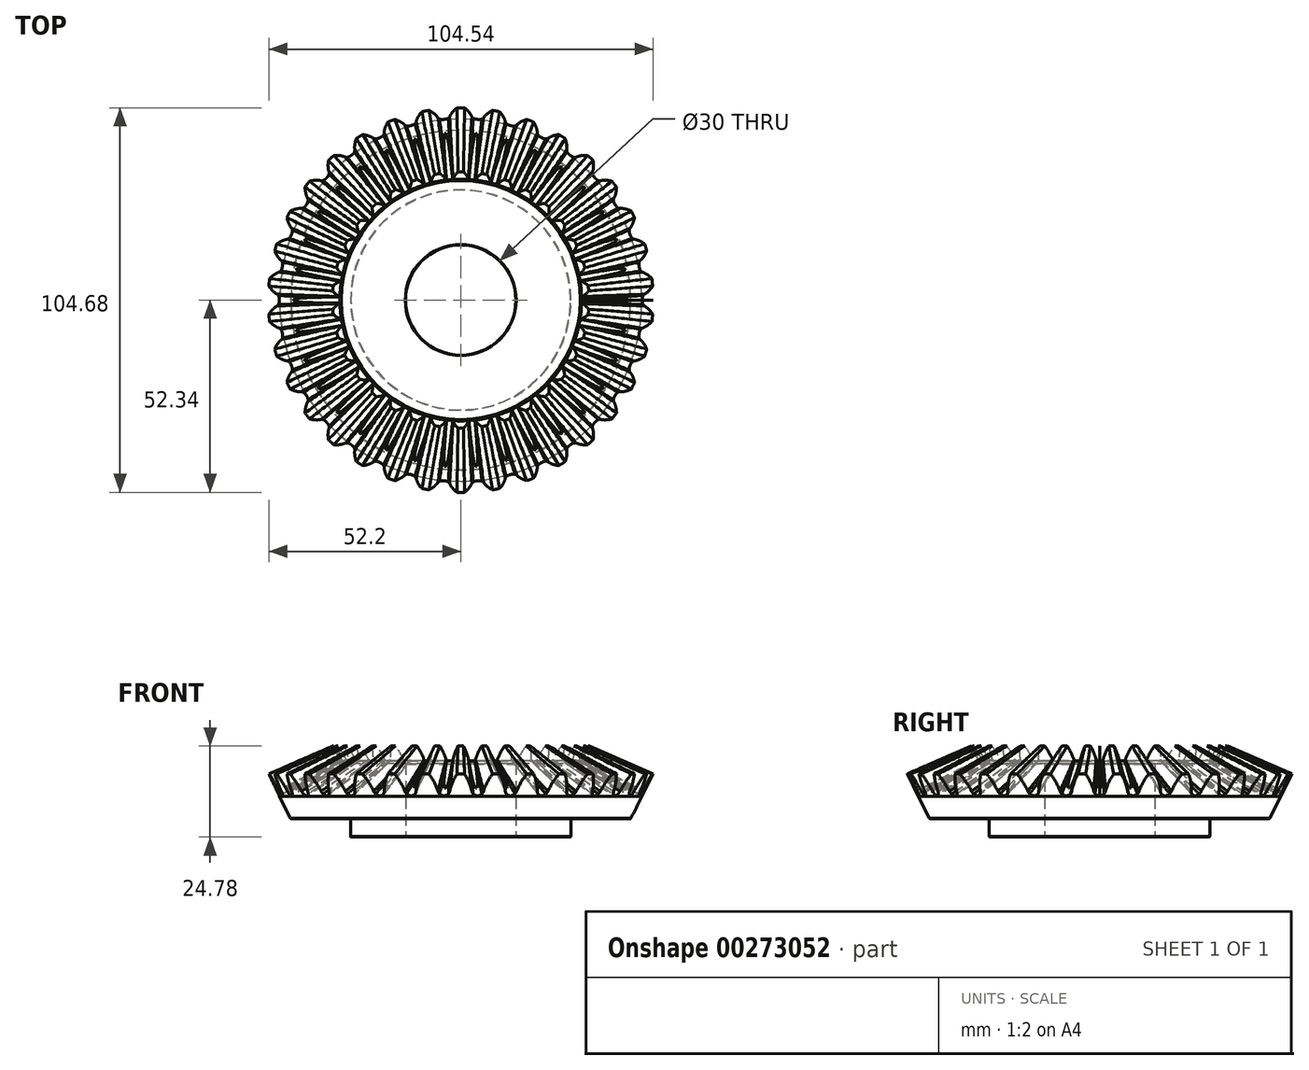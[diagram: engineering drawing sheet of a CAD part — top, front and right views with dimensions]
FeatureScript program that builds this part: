
annotation { "Feature Type Name" : "Feature", "Feature Type Description" : "" }
export const myFeature = defineFeature(function(context is Context, id is Id, definition is map)
    precondition{}
    {
        {
            var Q0;
            Q0=qCreatedBy(makeId("Front.planeOp"),FACE);
            var sketch = newSketch(context, id + "F0", { "sketchPlane" : qUnion([Q0])});
            skLineSegment(sketch, "E0", {"start": v(0, 35) * mm, "end": v(57.54, 6.23) * mm, "construction": true});
            skLineSegment(sketch, "E1", {"start": v(0, 35) * mm, "end": v(0, 0) * mm, "construction": true});
            skLineSegment(sketch, "E2", {"start": v(32.89, 15.76) * mm, "end": v(49.32, 6.14) * mm});
            skLineSegment(sketch, "E3", {"start": v(0, 0) * mm, "end": v(46.25, 0) * mm, "construction": true});
            skLineSegment(sketch, "E4", {"start": v(49.32, 6.14) * mm, "end": v(52.35, 12.18) * mm});
            skLineSegment(sketch, "E5", {"start": v(52.34, 12.18) * mm, "end": v(34.9, 19.78) * mm});
            skLineSegment(sketch, "E6", {"start": v(32.5, 15) * mm, "end": v(0, 15) * mm, "construction": true});
            skLineSegment(sketch, "E7", {"start": v(49.32, 6.14) * mm, "end": v(46.25, 0) * mm, "construction": true});
            skLineSegment(sketch, "E8", {"start": v(32.89, 15.76) * mm, "end": v(32.5, 15) * mm, "construction": true});
            skLineSegment(sketch, "E9", {"start": v(34.9, 19.78) * mm, "end": v(32.89, 15.76) * mm});
            skSolve(sketch);
        }
        {
            var Q0;
            Q0 = qSketchRegion(id + "F0", true);
            var Q1;
            Q1=sQuery(id+"F0.wireOp",EDGE,"E1");
            revolve(context, id + "F1", {"entities" : qUnion([Q0]), "axis" : qUnion([Q1]), "revolveType" : RevolveType.FULL});
        }
        {
            var Q0;
            Q0=qCreatedBy(makeId("Front.planeOp"),FACE);
            var sketch = newSketch(context, id + "F2", { "sketchPlane" : qUnion([Q0])});
            skLineSegment(sketch, "E10", {"start": v(0, 35) * mm, "end": v(0, 0) * mm, "construction": true});
            skLineSegment(sketch, "E11", {"start": v(0, 0) * mm, "end": v(46.25, 0) * mm});
            skLineSegment(sketch, "E12", {"start": v(32.5, 15) * mm, "end": v(0, 15) * mm});
            skLineSegment(sketch, "E13", {"start": v(49.32, 6.14) * mm, "end": v(46.25, 0) * mm});
            skLineSegment(sketch, "E14", {"start": v(32.89, 15.76) * mm, "end": v(32.5, 15) * mm});
            skLineSegment(sketch, "E15", {"start": v(32.89, 15.76) * mm, "end": v(49.32, 6.14) * mm});
            skLineSegment(sketch, "E16", {"start": v(0, 15) * mm, "end": v(0, 0) * mm});
            skSolve(sketch);
        }
        {
            var Q0;
            Q0 = qSketchRegion(id + "F2", true);
            var Q1;
            Q1=sQuery(id+"F2.wireOp",EDGE,"E10");
            revolve(context, id + "F3", {"entities" : qUnion([Q0]), "axis" : qUnion([Q1]), "revolveType" : RevolveType.FULL});
        }
        {
            var Q0;
            Q0 = qSketchRegion(id + "F0", true);
            extrude(context, id + "F4", {"entities" : qUnion([Q0]), "depth" : 0.01 * mm, "hasSecondDirection" : true, "secondDirectionOppositeDirection" : true, "secondDirectionDepth" : 0.01 * mm});
        }
        {
            var Q0;
            Q0=makeQuery(id+"F4.opExtrude","SWEPT_FACE",FACE,{"disambiguationData":[OSD([sQuery(id+"F0.wireOp",EDGE,"E4")])]});
            cPlane(context, id + "F5", {"entities" : qUnion([Q0]), "cplaneType" : CPlaneType.OFFSET, "offset" : 0 * mm, "width" : 150 * mm, "height" : 150 * mm});
        }
        {
            var Q0;
            Q0=qCreatedBy(id+"F5.planeOp",FACE);
            var sketch = newSketch(context, id + "F6", { "sketchPlane" : qUnion([Q0])});
            skPoint(sketch, "E17.center", {"position": v(0, 0) * mm});
            skLineSegment(sketch, "E17.anchor2", {"start": v(0, 0) * mm, "end": v(0, 27.7) * mm, "construction": true});
            skLineSegment(sketch, "E18", {"start": v(0, 27.7) * mm, "end": v(0, 34.3) * mm, "construction": true});
            skLineSegment(sketch, "E19", {"start": v(-3.86, 34.3) * mm, "end": v(3.86, 34.3) * mm});
            skLineSegment(sketch, "E20", {"start": v(-0.18, 27.69) * mm, "end": v(0.18, 27.69) * mm});
            skArc(sketch, "E21", {"start": v(-1.58, 28.95) * mm, "mid": v(-2.5, 31.72) * mm, "end": v(-3.86, 34.3) * mm});
            skArc(sketch, "E22", {"start": v(-1.6, 29.04) * mm, "mid": v(-1.37, 28.44) * mm, "end": v(-0.96, 27.95) * mm});
            skArc(sketch, "E23", {"start": v(-1.21, 28.2) * mm, "mid": v(-0.76, 27.83) * mm, "end": v(-0.18, 27.69) * mm});
            skArc(sketch, "E24.MirrorCS", {"start": v(1.21, 28.2) * mm, "mid": v(0.76, 27.83) * mm, "end": v(0.18, 27.69) * mm});
            skArc(sketch, "E25.MirrorCS", {"start": v(1.6, 29.04) * mm, "mid": v(1.37, 28.44) * mm, "end": v(0.96, 27.95) * mm});
            skArc(sketch, "E26.MirrorCS", {"start": v(1.58, 28.95) * mm, "mid": v(2.5, 31.72) * mm, "end": v(3.86, 34.3) * mm});
            skSolve(sketch);
        }
        {
            var Q0;
            Q0 = qSketchRegion(id + "F6", true);
            extrude(context, id + "F7", {"entities" : qUnion([Q0]), "oppositeDirection" : true, "depth" : 20 * mm, "hasDraft" : true, "draftAngle" : 2 * degree, "draftPullDirection" : true});
        }
        {
            var Q0;
            Q0=makeQuery(id+"F7.opExtrude","SWEPT_BODY",BODY,{"disambiguationData":[OSD([sQuery(id+"F6.wireOp",EDGE,"E19"),sQuery(id+"F6.wireOp",EDGE,"E20"),sQuery(id+"F6.wireOp",EDGE,"E21"),sQuery(id+"F6.wireOp",EDGE,"E22"),sQuery(id+"F6.wireOp",EDGE,"E23"),sQuery(id+"F6.wireOp",EDGE,"E24.MirrorCS"),sQuery(id+"F6.wireOp",EDGE,"E25.MirrorCS"),sQuery(id+"F6.wireOp",EDGE,"E26.MirrorCS")])]});
            var Q1;
            Q1=makeQuery(id+"F3.opRevolve","SWEPT_EDGE",EDGE,{"disambiguationData":[OSD([sQuery(id+"F2.wireOp",EDGE,"E11"),sQuery(id+"F2.wireOp",EDGE,"E13")])]});
            circularPattern(context, id + "F8", {"entities" : qUnion([Q0]), "axis" : qUnion([Q1]), "angle" : 360 * degree, "instanceCount" : 34, "equalSpace" : true});
        }
        {
            var Q0;
            Q0=makeQuery(id+"F8.opPattern","COPY",BODY,{"derivedFrom":makeQuery(id+"F7.opExtrude","SWEPT_BODY",BODY,{"disambiguationData":[OSD([sQuery(id+"F6.wireOp",EDGE,"E19"),sQuery(id+"F6.wireOp",EDGE,"E20"),sQuery(id+"F6.wireOp",EDGE,"E21"),sQuery(id+"F6.wireOp",EDGE,"E22"),sQuery(id+"F6.wireOp",EDGE,"E23"),sQuery(id+"F6.wireOp",EDGE,"E24.MirrorCS"),sQuery(id+"F6.wireOp",EDGE,"E25.MirrorCS"),sQuery(id+"F6.wireOp",EDGE,"E26.MirrorCS")])]}),"instanceName":"26"});
            var Q1;
            Q1=makeQuery(id+"F8.opPattern","COPY",BODY,{"derivedFrom":makeQuery(id+"F7.opExtrude","SWEPT_BODY",BODY,{"disambiguationData":[OSD([sQuery(id+"F6.wireOp",EDGE,"E19"),sQuery(id+"F6.wireOp",EDGE,"E20"),sQuery(id+"F6.wireOp",EDGE,"E21"),sQuery(id+"F6.wireOp",EDGE,"E22"),sQuery(id+"F6.wireOp",EDGE,"E23"),sQuery(id+"F6.wireOp",EDGE,"E24.MirrorCS"),sQuery(id+"F6.wireOp",EDGE,"E25.MirrorCS"),sQuery(id+"F6.wireOp",EDGE,"E26.MirrorCS")])]}),"instanceName":"27"});
            var Q2;
            Q2=makeQuery(id+"F8.opPattern","COPY",BODY,{"derivedFrom":makeQuery(id+"F7.opExtrude","SWEPT_BODY",BODY,{"disambiguationData":[OSD([sQuery(id+"F6.wireOp",EDGE,"E19"),sQuery(id+"F6.wireOp",EDGE,"E20"),sQuery(id+"F6.wireOp",EDGE,"E21"),sQuery(id+"F6.wireOp",EDGE,"E22"),sQuery(id+"F6.wireOp",EDGE,"E23"),sQuery(id+"F6.wireOp",EDGE,"E24.MirrorCS"),sQuery(id+"F6.wireOp",EDGE,"E25.MirrorCS"),sQuery(id+"F6.wireOp",EDGE,"E26.MirrorCS")])]}),"instanceName":"28"});
            var Q3;
            Q3=makeQuery(id+"F8.opPattern","COPY",BODY,{"derivedFrom":makeQuery(id+"F7.opExtrude","SWEPT_BODY",BODY,{"disambiguationData":[OSD([sQuery(id+"F6.wireOp",EDGE,"E19"),sQuery(id+"F6.wireOp",EDGE,"E20"),sQuery(id+"F6.wireOp",EDGE,"E21"),sQuery(id+"F6.wireOp",EDGE,"E22"),sQuery(id+"F6.wireOp",EDGE,"E23"),sQuery(id+"F6.wireOp",EDGE,"E24.MirrorCS"),sQuery(id+"F6.wireOp",EDGE,"E25.MirrorCS"),sQuery(id+"F6.wireOp",EDGE,"E26.MirrorCS")])]}),"instanceName":"29"});
            var Q4;
            Q4=makeQuery(id+"F8.opPattern","COPY",BODY,{"derivedFrom":makeQuery(id+"F7.opExtrude","SWEPT_BODY",BODY,{"disambiguationData":[OSD([sQuery(id+"F6.wireOp",EDGE,"E19"),sQuery(id+"F6.wireOp",EDGE,"E20"),sQuery(id+"F6.wireOp",EDGE,"E21"),sQuery(id+"F6.wireOp",EDGE,"E22"),sQuery(id+"F6.wireOp",EDGE,"E23"),sQuery(id+"F6.wireOp",EDGE,"E24.MirrorCS"),sQuery(id+"F6.wireOp",EDGE,"E25.MirrorCS"),sQuery(id+"F6.wireOp",EDGE,"E26.MirrorCS")])]}),"instanceName":"30"});
            var Q5;
            Q5=makeQuery(id+"F8.opPattern","COPY",BODY,{"derivedFrom":makeQuery(id+"F7.opExtrude","SWEPT_BODY",BODY,{"disambiguationData":[OSD([sQuery(id+"F6.wireOp",EDGE,"E19"),sQuery(id+"F6.wireOp",EDGE,"E20"),sQuery(id+"F6.wireOp",EDGE,"E21"),sQuery(id+"F6.wireOp",EDGE,"E22"),sQuery(id+"F6.wireOp",EDGE,"E23"),sQuery(id+"F6.wireOp",EDGE,"E24.MirrorCS"),sQuery(id+"F6.wireOp",EDGE,"E25.MirrorCS"),sQuery(id+"F6.wireOp",EDGE,"E26.MirrorCS")])]}),"instanceName":"31"});
            var Q6;
            Q6=makeQuery(id+"F8.opPattern","COPY",BODY,{"derivedFrom":makeQuery(id+"F7.opExtrude","SWEPT_BODY",BODY,{"disambiguationData":[OSD([sQuery(id+"F6.wireOp",EDGE,"E19"),sQuery(id+"F6.wireOp",EDGE,"E20"),sQuery(id+"F6.wireOp",EDGE,"E21"),sQuery(id+"F6.wireOp",EDGE,"E22"),sQuery(id+"F6.wireOp",EDGE,"E23"),sQuery(id+"F6.wireOp",EDGE,"E24.MirrorCS"),sQuery(id+"F6.wireOp",EDGE,"E25.MirrorCS"),sQuery(id+"F6.wireOp",EDGE,"E26.MirrorCS")])]}),"instanceName":"32"});
            var Q7;
            Q7=makeQuery(id+"F8.opPattern","COPY",BODY,{"derivedFrom":makeQuery(id+"F7.opExtrude","SWEPT_BODY",BODY,{"disambiguationData":[OSD([sQuery(id+"F6.wireOp",EDGE,"E19"),sQuery(id+"F6.wireOp",EDGE,"E20"),sQuery(id+"F6.wireOp",EDGE,"E21"),sQuery(id+"F6.wireOp",EDGE,"E22"),sQuery(id+"F6.wireOp",EDGE,"E23"),sQuery(id+"F6.wireOp",EDGE,"E24.MirrorCS"),sQuery(id+"F6.wireOp",EDGE,"E25.MirrorCS"),sQuery(id+"F6.wireOp",EDGE,"E26.MirrorCS")])]}),"instanceName":"33"});
            var Q8;
            Q8=makeQuery(id+"F7.opExtrude","SWEPT_BODY",BODY,{"disambiguationData":[OSD([sQuery(id+"F6.wireOp",EDGE,"E19"),sQuery(id+"F6.wireOp",EDGE,"E20"),sQuery(id+"F6.wireOp",EDGE,"E21"),sQuery(id+"F6.wireOp",EDGE,"E22"),sQuery(id+"F6.wireOp",EDGE,"E23"),sQuery(id+"F6.wireOp",EDGE,"E24.MirrorCS"),sQuery(id+"F6.wireOp",EDGE,"E25.MirrorCS"),sQuery(id+"F6.wireOp",EDGE,"E26.MirrorCS")])]});
            var Q9;
            Q9=makeQuery(id+"F8.opPattern","COPY",BODY,{"derivedFrom":makeQuery(id+"F7.opExtrude","SWEPT_BODY",BODY,{"disambiguationData":[OSD([sQuery(id+"F6.wireOp",EDGE,"E19"),sQuery(id+"F6.wireOp",EDGE,"E20"),sQuery(id+"F6.wireOp",EDGE,"E21"),sQuery(id+"F6.wireOp",EDGE,"E22"),sQuery(id+"F6.wireOp",EDGE,"E23"),sQuery(id+"F6.wireOp",EDGE,"E24.MirrorCS"),sQuery(id+"F6.wireOp",EDGE,"E25.MirrorCS"),sQuery(id+"F6.wireOp",EDGE,"E26.MirrorCS")])]}),"instanceName":"1"});
            var Q10;
            Q10=makeQuery(id+"F8.opPattern","COPY",BODY,{"derivedFrom":makeQuery(id+"F7.opExtrude","SWEPT_BODY",BODY,{"disambiguationData":[OSD([sQuery(id+"F6.wireOp",EDGE,"E19"),sQuery(id+"F6.wireOp",EDGE,"E20"),sQuery(id+"F6.wireOp",EDGE,"E21"),sQuery(id+"F6.wireOp",EDGE,"E22"),sQuery(id+"F6.wireOp",EDGE,"E23"),sQuery(id+"F6.wireOp",EDGE,"E24.MirrorCS"),sQuery(id+"F6.wireOp",EDGE,"E25.MirrorCS"),sQuery(id+"F6.wireOp",EDGE,"E26.MirrorCS")])]}),"instanceName":"2"});
            var Q11;
            Q11=makeQuery(id+"F8.opPattern","COPY",BODY,{"derivedFrom":makeQuery(id+"F7.opExtrude","SWEPT_BODY",BODY,{"disambiguationData":[OSD([sQuery(id+"F6.wireOp",EDGE,"E19"),sQuery(id+"F6.wireOp",EDGE,"E20"),sQuery(id+"F6.wireOp",EDGE,"E21"),sQuery(id+"F6.wireOp",EDGE,"E22"),sQuery(id+"F6.wireOp",EDGE,"E23"),sQuery(id+"F6.wireOp",EDGE,"E24.MirrorCS"),sQuery(id+"F6.wireOp",EDGE,"E25.MirrorCS"),sQuery(id+"F6.wireOp",EDGE,"E26.MirrorCS")])]}),"instanceName":"3"});
            var Q12;
            Q12=makeQuery(id+"F8.opPattern","COPY",BODY,{"derivedFrom":makeQuery(id+"F7.opExtrude","SWEPT_BODY",BODY,{"disambiguationData":[OSD([sQuery(id+"F6.wireOp",EDGE,"E19"),sQuery(id+"F6.wireOp",EDGE,"E20"),sQuery(id+"F6.wireOp",EDGE,"E21"),sQuery(id+"F6.wireOp",EDGE,"E22"),sQuery(id+"F6.wireOp",EDGE,"E23"),sQuery(id+"F6.wireOp",EDGE,"E24.MirrorCS"),sQuery(id+"F6.wireOp",EDGE,"E25.MirrorCS"),sQuery(id+"F6.wireOp",EDGE,"E26.MirrorCS")])]}),"instanceName":"4"});
            var Q13;
            Q13=makeQuery(id+"F8.opPattern","COPY",BODY,{"derivedFrom":makeQuery(id+"F7.opExtrude","SWEPT_BODY",BODY,{"disambiguationData":[OSD([sQuery(id+"F6.wireOp",EDGE,"E19"),sQuery(id+"F6.wireOp",EDGE,"E20"),sQuery(id+"F6.wireOp",EDGE,"E21"),sQuery(id+"F6.wireOp",EDGE,"E22"),sQuery(id+"F6.wireOp",EDGE,"E23"),sQuery(id+"F6.wireOp",EDGE,"E24.MirrorCS"),sQuery(id+"F6.wireOp",EDGE,"E25.MirrorCS"),sQuery(id+"F6.wireOp",EDGE,"E26.MirrorCS")])]}),"instanceName":"5"});
            var Q14;
            Q14=makeQuery(id+"F8.opPattern","COPY",BODY,{"derivedFrom":makeQuery(id+"F7.opExtrude","SWEPT_BODY",BODY,{"disambiguationData":[OSD([sQuery(id+"F6.wireOp",EDGE,"E19"),sQuery(id+"F6.wireOp",EDGE,"E20"),sQuery(id+"F6.wireOp",EDGE,"E21"),sQuery(id+"F6.wireOp",EDGE,"E22"),sQuery(id+"F6.wireOp",EDGE,"E23"),sQuery(id+"F6.wireOp",EDGE,"E24.MirrorCS"),sQuery(id+"F6.wireOp",EDGE,"E25.MirrorCS"),sQuery(id+"F6.wireOp",EDGE,"E26.MirrorCS")])]}),"instanceName":"6"});
            var Q15;
            Q15=makeQuery(id+"F8.opPattern","COPY",BODY,{"derivedFrom":makeQuery(id+"F7.opExtrude","SWEPT_BODY",BODY,{"disambiguationData":[OSD([sQuery(id+"F6.wireOp",EDGE,"E19"),sQuery(id+"F6.wireOp",EDGE,"E20"),sQuery(id+"F6.wireOp",EDGE,"E21"),sQuery(id+"F6.wireOp",EDGE,"E22"),sQuery(id+"F6.wireOp",EDGE,"E23"),sQuery(id+"F6.wireOp",EDGE,"E24.MirrorCS"),sQuery(id+"F6.wireOp",EDGE,"E25.MirrorCS"),sQuery(id+"F6.wireOp",EDGE,"E26.MirrorCS")])]}),"instanceName":"7"});
            var Q16;
            Q16=makeQuery(id+"F8.opPattern","COPY",BODY,{"derivedFrom":makeQuery(id+"F7.opExtrude","SWEPT_BODY",BODY,{"disambiguationData":[OSD([sQuery(id+"F6.wireOp",EDGE,"E19"),sQuery(id+"F6.wireOp",EDGE,"E20"),sQuery(id+"F6.wireOp",EDGE,"E21"),sQuery(id+"F6.wireOp",EDGE,"E22"),sQuery(id+"F6.wireOp",EDGE,"E23"),sQuery(id+"F6.wireOp",EDGE,"E24.MirrorCS"),sQuery(id+"F6.wireOp",EDGE,"E25.MirrorCS"),sQuery(id+"F6.wireOp",EDGE,"E26.MirrorCS")])]}),"instanceName":"25"});
            var Q17;
            Q17=makeQuery(id+"F8.opPattern","COPY",BODY,{"derivedFrom":makeQuery(id+"F7.opExtrude","SWEPT_BODY",BODY,{"disambiguationData":[OSD([sQuery(id+"F6.wireOp",EDGE,"E19"),sQuery(id+"F6.wireOp",EDGE,"E20"),sQuery(id+"F6.wireOp",EDGE,"E21"),sQuery(id+"F6.wireOp",EDGE,"E22"),sQuery(id+"F6.wireOp",EDGE,"E23"),sQuery(id+"F6.wireOp",EDGE,"E24.MirrorCS"),sQuery(id+"F6.wireOp",EDGE,"E25.MirrorCS"),sQuery(id+"F6.wireOp",EDGE,"E26.MirrorCS")])]}),"instanceName":"24"});
            var Q18;
            Q18=makeQuery(id+"F8.opPattern","COPY",BODY,{"derivedFrom":makeQuery(id+"F7.opExtrude","SWEPT_BODY",BODY,{"disambiguationData":[OSD([sQuery(id+"F6.wireOp",EDGE,"E19"),sQuery(id+"F6.wireOp",EDGE,"E20"),sQuery(id+"F6.wireOp",EDGE,"E21"),sQuery(id+"F6.wireOp",EDGE,"E22"),sQuery(id+"F6.wireOp",EDGE,"E23"),sQuery(id+"F6.wireOp",EDGE,"E24.MirrorCS"),sQuery(id+"F6.wireOp",EDGE,"E25.MirrorCS"),sQuery(id+"F6.wireOp",EDGE,"E26.MirrorCS")])]}),"instanceName":"23"});
            var Q19;
            Q19=makeQuery(id+"F8.opPattern","COPY",BODY,{"derivedFrom":makeQuery(id+"F7.opExtrude","SWEPT_BODY",BODY,{"disambiguationData":[OSD([sQuery(id+"F6.wireOp",EDGE,"E19"),sQuery(id+"F6.wireOp",EDGE,"E20"),sQuery(id+"F6.wireOp",EDGE,"E21"),sQuery(id+"F6.wireOp",EDGE,"E22"),sQuery(id+"F6.wireOp",EDGE,"E23"),sQuery(id+"F6.wireOp",EDGE,"E24.MirrorCS"),sQuery(id+"F6.wireOp",EDGE,"E25.MirrorCS"),sQuery(id+"F6.wireOp",EDGE,"E26.MirrorCS")])]}),"instanceName":"22"});
            var Q20;
            Q20=makeQuery(id+"F8.opPattern","COPY",BODY,{"derivedFrom":makeQuery(id+"F7.opExtrude","SWEPT_BODY",BODY,{"disambiguationData":[OSD([sQuery(id+"F6.wireOp",EDGE,"E19"),sQuery(id+"F6.wireOp",EDGE,"E20"),sQuery(id+"F6.wireOp",EDGE,"E21"),sQuery(id+"F6.wireOp",EDGE,"E22"),sQuery(id+"F6.wireOp",EDGE,"E23"),sQuery(id+"F6.wireOp",EDGE,"E24.MirrorCS"),sQuery(id+"F6.wireOp",EDGE,"E25.MirrorCS"),sQuery(id+"F6.wireOp",EDGE,"E26.MirrorCS")])]}),"instanceName":"21"});
            var Q21;
            Q21=makeQuery(id+"F8.opPattern","COPY",BODY,{"derivedFrom":makeQuery(id+"F7.opExtrude","SWEPT_BODY",BODY,{"disambiguationData":[OSD([sQuery(id+"F6.wireOp",EDGE,"E19"),sQuery(id+"F6.wireOp",EDGE,"E20"),sQuery(id+"F6.wireOp",EDGE,"E21"),sQuery(id+"F6.wireOp",EDGE,"E22"),sQuery(id+"F6.wireOp",EDGE,"E23"),sQuery(id+"F6.wireOp",EDGE,"E24.MirrorCS"),sQuery(id+"F6.wireOp",EDGE,"E25.MirrorCS"),sQuery(id+"F6.wireOp",EDGE,"E26.MirrorCS")])]}),"instanceName":"20"});
            var Q22;
            Q22=makeQuery(id+"F8.opPattern","COPY",BODY,{"derivedFrom":makeQuery(id+"F7.opExtrude","SWEPT_BODY",BODY,{"disambiguationData":[OSD([sQuery(id+"F6.wireOp",EDGE,"E19"),sQuery(id+"F6.wireOp",EDGE,"E20"),sQuery(id+"F6.wireOp",EDGE,"E21"),sQuery(id+"F6.wireOp",EDGE,"E22"),sQuery(id+"F6.wireOp",EDGE,"E23"),sQuery(id+"F6.wireOp",EDGE,"E24.MirrorCS"),sQuery(id+"F6.wireOp",EDGE,"E25.MirrorCS"),sQuery(id+"F6.wireOp",EDGE,"E26.MirrorCS")])]}),"instanceName":"19"});
            var Q23;
            Q23=makeQuery(id+"F8.opPattern","COPY",BODY,{"derivedFrom":makeQuery(id+"F7.opExtrude","SWEPT_BODY",BODY,{"disambiguationData":[OSD([sQuery(id+"F6.wireOp",EDGE,"E19"),sQuery(id+"F6.wireOp",EDGE,"E20"),sQuery(id+"F6.wireOp",EDGE,"E21"),sQuery(id+"F6.wireOp",EDGE,"E22"),sQuery(id+"F6.wireOp",EDGE,"E23"),sQuery(id+"F6.wireOp",EDGE,"E24.MirrorCS"),sQuery(id+"F6.wireOp",EDGE,"E25.MirrorCS"),sQuery(id+"F6.wireOp",EDGE,"E26.MirrorCS")])]}),"instanceName":"18"});
            var Q24;
            Q24=makeQuery(id+"F8.opPattern","COPY",BODY,{"derivedFrom":makeQuery(id+"F7.opExtrude","SWEPT_BODY",BODY,{"disambiguationData":[OSD([sQuery(id+"F6.wireOp",EDGE,"E19"),sQuery(id+"F6.wireOp",EDGE,"E20"),sQuery(id+"F6.wireOp",EDGE,"E21"),sQuery(id+"F6.wireOp",EDGE,"E22"),sQuery(id+"F6.wireOp",EDGE,"E23"),sQuery(id+"F6.wireOp",EDGE,"E24.MirrorCS"),sQuery(id+"F6.wireOp",EDGE,"E25.MirrorCS"),sQuery(id+"F6.wireOp",EDGE,"E26.MirrorCS")])]}),"instanceName":"17"});
            var Q25;
            Q25=makeQuery(id+"F8.opPattern","COPY",BODY,{"derivedFrom":makeQuery(id+"F7.opExtrude","SWEPT_BODY",BODY,{"disambiguationData":[OSD([sQuery(id+"F6.wireOp",EDGE,"E19"),sQuery(id+"F6.wireOp",EDGE,"E20"),sQuery(id+"F6.wireOp",EDGE,"E21"),sQuery(id+"F6.wireOp",EDGE,"E22"),sQuery(id+"F6.wireOp",EDGE,"E23"),sQuery(id+"F6.wireOp",EDGE,"E24.MirrorCS"),sQuery(id+"F6.wireOp",EDGE,"E25.MirrorCS"),sQuery(id+"F6.wireOp",EDGE,"E26.MirrorCS")])]}),"instanceName":"16"});
            var Q26;
            Q26=makeQuery(id+"F8.opPattern","COPY",BODY,{"derivedFrom":makeQuery(id+"F7.opExtrude","SWEPT_BODY",BODY,{"disambiguationData":[OSD([sQuery(id+"F6.wireOp",EDGE,"E19"),sQuery(id+"F6.wireOp",EDGE,"E20"),sQuery(id+"F6.wireOp",EDGE,"E21"),sQuery(id+"F6.wireOp",EDGE,"E22"),sQuery(id+"F6.wireOp",EDGE,"E23"),sQuery(id+"F6.wireOp",EDGE,"E24.MirrorCS"),sQuery(id+"F6.wireOp",EDGE,"E25.MirrorCS"),sQuery(id+"F6.wireOp",EDGE,"E26.MirrorCS")])]}),"instanceName":"15"});
            var Q27;
            Q27=makeQuery(id+"F8.opPattern","COPY",BODY,{"derivedFrom":makeQuery(id+"F7.opExtrude","SWEPT_BODY",BODY,{"disambiguationData":[OSD([sQuery(id+"F6.wireOp",EDGE,"E19"),sQuery(id+"F6.wireOp",EDGE,"E20"),sQuery(id+"F6.wireOp",EDGE,"E21"),sQuery(id+"F6.wireOp",EDGE,"E22"),sQuery(id+"F6.wireOp",EDGE,"E23"),sQuery(id+"F6.wireOp",EDGE,"E24.MirrorCS"),sQuery(id+"F6.wireOp",EDGE,"E25.MirrorCS"),sQuery(id+"F6.wireOp",EDGE,"E26.MirrorCS")])]}),"instanceName":"14"});
            var Q28;
            Q28=makeQuery(id+"F8.opPattern","COPY",BODY,{"derivedFrom":makeQuery(id+"F7.opExtrude","SWEPT_BODY",BODY,{"disambiguationData":[OSD([sQuery(id+"F6.wireOp",EDGE,"E19"),sQuery(id+"F6.wireOp",EDGE,"E20"),sQuery(id+"F6.wireOp",EDGE,"E21"),sQuery(id+"F6.wireOp",EDGE,"E22"),sQuery(id+"F6.wireOp",EDGE,"E23"),sQuery(id+"F6.wireOp",EDGE,"E24.MirrorCS"),sQuery(id+"F6.wireOp",EDGE,"E25.MirrorCS"),sQuery(id+"F6.wireOp",EDGE,"E26.MirrorCS")])]}),"instanceName":"13"});
            var Q29;
            Q29=makeQuery(id+"F8.opPattern","COPY",BODY,{"derivedFrom":makeQuery(id+"F7.opExtrude","SWEPT_BODY",BODY,{"disambiguationData":[OSD([sQuery(id+"F6.wireOp",EDGE,"E19"),sQuery(id+"F6.wireOp",EDGE,"E20"),sQuery(id+"F6.wireOp",EDGE,"E21"),sQuery(id+"F6.wireOp",EDGE,"E22"),sQuery(id+"F6.wireOp",EDGE,"E23"),sQuery(id+"F6.wireOp",EDGE,"E24.MirrorCS"),sQuery(id+"F6.wireOp",EDGE,"E25.MirrorCS"),sQuery(id+"F6.wireOp",EDGE,"E26.MirrorCS")])]}),"instanceName":"12"});
            var Q30;
            Q30=makeQuery(id+"F8.opPattern","COPY",BODY,{"derivedFrom":makeQuery(id+"F7.opExtrude","SWEPT_BODY",BODY,{"disambiguationData":[OSD([sQuery(id+"F6.wireOp",EDGE,"E19"),sQuery(id+"F6.wireOp",EDGE,"E20"),sQuery(id+"F6.wireOp",EDGE,"E21"),sQuery(id+"F6.wireOp",EDGE,"E22"),sQuery(id+"F6.wireOp",EDGE,"E23"),sQuery(id+"F6.wireOp",EDGE,"E24.MirrorCS"),sQuery(id+"F6.wireOp",EDGE,"E25.MirrorCS"),sQuery(id+"F6.wireOp",EDGE,"E26.MirrorCS")])]}),"instanceName":"11"});
            var Q31;
            Q31=makeQuery(id+"F8.opPattern","COPY",BODY,{"derivedFrom":makeQuery(id+"F7.opExtrude","SWEPT_BODY",BODY,{"disambiguationData":[OSD([sQuery(id+"F6.wireOp",EDGE,"E19"),sQuery(id+"F6.wireOp",EDGE,"E20"),sQuery(id+"F6.wireOp",EDGE,"E21"),sQuery(id+"F6.wireOp",EDGE,"E22"),sQuery(id+"F6.wireOp",EDGE,"E23"),sQuery(id+"F6.wireOp",EDGE,"E24.MirrorCS"),sQuery(id+"F6.wireOp",EDGE,"E25.MirrorCS"),sQuery(id+"F6.wireOp",EDGE,"E26.MirrorCS")])]}),"instanceName":"10"});
            var Q32;
            Q32=makeQuery(id+"F8.opPattern","COPY",BODY,{"derivedFrom":makeQuery(id+"F7.opExtrude","SWEPT_BODY",BODY,{"disambiguationData":[OSD([sQuery(id+"F6.wireOp",EDGE,"E19"),sQuery(id+"F6.wireOp",EDGE,"E20"),sQuery(id+"F6.wireOp",EDGE,"E21"),sQuery(id+"F6.wireOp",EDGE,"E22"),sQuery(id+"F6.wireOp",EDGE,"E23"),sQuery(id+"F6.wireOp",EDGE,"E24.MirrorCS"),sQuery(id+"F6.wireOp",EDGE,"E25.MirrorCS"),sQuery(id+"F6.wireOp",EDGE,"E26.MirrorCS")])]}),"instanceName":"9"});
            var Q33;
            Q33=makeQuery(id+"F8.opPattern","COPY",BODY,{"derivedFrom":makeQuery(id+"F7.opExtrude","SWEPT_BODY",BODY,{"disambiguationData":[OSD([sQuery(id+"F6.wireOp",EDGE,"E19"),sQuery(id+"F6.wireOp",EDGE,"E20"),sQuery(id+"F6.wireOp",EDGE,"E21"),sQuery(id+"F6.wireOp",EDGE,"E22"),sQuery(id+"F6.wireOp",EDGE,"E23"),sQuery(id+"F6.wireOp",EDGE,"E24.MirrorCS"),sQuery(id+"F6.wireOp",EDGE,"E25.MirrorCS"),sQuery(id+"F6.wireOp",EDGE,"E26.MirrorCS")])]}),"instanceName":"8"});
            var Q34;
            Q34=makeQuery(id+"F1.opRevolve","SWEPT_BODY",BODY,{"disambiguationData":[OSD([sQuery(id+"F0.wireOp",EDGE,"E2"),sQuery(id+"F0.wireOp",EDGE,"E4"),sQuery(id+"F0.wireOp",EDGE,"E5"),sQuery(id+"F0.wireOp",EDGE,"E9")])]});
            booleanBodies(context, id + "F9", {"operationType" : BooleanOperationType.SUBTRACTION, "tools" : qUnion([Q0, Q1, Q2, Q3, Q4, Q5, Q6, Q7, Q8, Q9, Q10, Q11, Q12, Q13, Q14, Q15, Q16, Q17, Q18, Q19, Q20, Q21, Q22, Q23, Q24, Q25, Q26, Q27, Q28, Q29, Q30, Q31, Q32, Q33]), "targets" : qUnion([Q34])});
        }
        {
            var Q0;
            Q0=makeQuery(id+"F3.opRevolve","SWEPT_FACE",FACE,{"disambiguationData":[OSD([sQuery(id+"F2.wireOp",EDGE,"E11")])]});
            var sketch = newSketch(context, id + "F10", { "sketchPlane" : qUnion([Q0])});
            skCircle(sketch, "E27", {"center": v(0, 0) * mm, "radius": 30 * mm});
            skSolve(sketch);
        }
        {
            var Q0;
            Q0 = qSketchRegion(id + "F10", true);
            extrude(context, id + "F11", {"entities" : qUnion([Q0]), "operationType" : NewBodyOperationType.ADD, "depth" : 5 * mm});
        }
        {
            var Q0;
            Q0=makeQuery(id+"F11.opExtrude","CAP_FACE",FACE,{"disambiguationData":[OSD([sQuery(id+"F10.wireOp",EDGE,"E27")])],"isStart":false});
            var sketch = newSketch(context, id + "F12", { "sketchPlane" : qUnion([Q0])});
            skCircle(sketch, "E28", {"center": v(0, 0) * mm, "radius": 15 * mm});
            skSolve(sketch);
        }
        {
            var Q0;
            Q0 = qSketchRegion(id + "F12", true);
            extrude(context, id + "F13", {"entities" : qUnion([Q0]), "operationType" : NewBodyOperationType.REMOVE, "oppositeDirection" : true, "depth" : 25 * mm});
        }
        {
            var Q0;
            Q0=makeQuery(id+"F13.boolean.opBoolean","INTERSECT",EDGE,{"derivedFrom":[makeQuery(id+"F3.opRevolve","SWEPT_FACE",FACE,{"disambiguationData":[OSD([sQuery(id+"F2.wireOp",EDGE,"E12")])]}),makeQuery(id+"F13.opExtrude","SWEPT_FACE",FACE,{"disambiguationData":[OSD([sQuery(id+"F12.wireOp",EDGE,"E28")])]})]});
            var Q1;
            Q1=makeQuery(id+"F13.boolean.opBoolean","COPY",EDGE,{"derivedFrom":makeQuery(id+"F13.opExtrude","CAP_EDGE",EDGE,{"disambiguationData":[OSD([sQuery(id+"F12.wireOp",EDGE,"E28")])],"isStart":true})});
            var Q2;
            Q2=makeQuery(id+"F11.opExtrude","CAP_EDGE",EDGE,{"disambiguationData":[OSD([sQuery(id+"F10.wireOp",EDGE,"E27")])],"isStart":false});
            var Q3;
            Q3=makeQuery(id+"F3.opRevolve","SWEPT_EDGE",EDGE,{"disambiguationData":[OSD([sQuery(id+"F2.wireOp",EDGE,"E11"),sQuery(id+"F2.wireOp",EDGE,"E13")])]});
            chamfer(context, id + "F14", {"entities" : qUnion([Q0, Q1, Q2, Q3]), "width" : 0.1 * mm, "tangentPropagation" : true});
        }
    });
